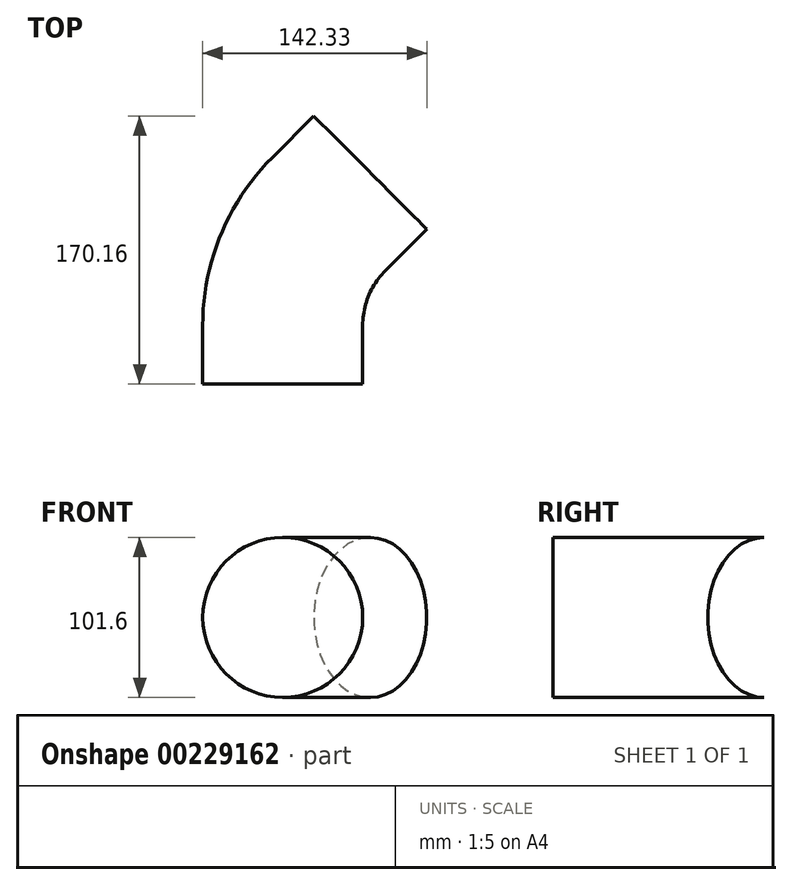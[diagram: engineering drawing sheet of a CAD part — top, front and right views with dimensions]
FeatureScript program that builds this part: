
annotation { "Feature Type Name" : "Feature", "Feature Type Description" : "" }
export const myFeature = defineFeature(function(context is Context, id is Id, definition is map)
    precondition{}
    {
        {
            var Q0;
            Q0=qCreatedBy(makeId("Front.planeOp"),FACE);
            var sketch = newSketch(context, id + "F0", { "sketchPlane" : qUnion([Q0])});
            skCircle(sketch, "E0", {"center": v(1.47, 0) * mm, "radius": 50.8 * mm});
            skSolve(sketch);
        }
        {
            var Q0;
            Q0=qCreatedBy(makeId("Top.planeOp"),FACE);
            var sketch = newSketch(context, id + "F1", { "sketchPlane" : qUnion([Q0])});
            skLineSegment(sketch, "E1", {"start": v(0, 0) * mm, "end": v(0, 37.16) * mm});
            skLineSegment(sketch, "E2", {"start": v(29.76, 109) * mm, "end": v(56.04, 135.28) * mm});
            skPoint(sketch, "E3.visualSharp", {"position": v(0, 79.25) * mm});
            skArc(sketch, "E3.filletArc", {"start": v(29.76, 109) * mm, "mid": v(7.73, 76.04) * mm, "end": v(0, 37.16) * mm});
            skSolve(sketch);
        }
        {
            var Q0;
            Q0=makeQuery(id+"F0.imprint","IMPRINT",FACE,{"disambiguationData":[TD([[makeQuery(id+"F0.imprint","IMPRINT",EDGE,{"derivedFrom":sQuery(id+"F0.wireOp",EDGE,"E0")}),1.0]])]});
            var Q1;
            Q1=sQuery(id+"F1.wireOp",EDGE,"E1");
            var Q2;
            Q2=sQuery(id+"F1.wireOp",EDGE,"E3.filletArc");
            var Q3;
            Q3=sQuery(id+"F1.wireOp",EDGE,"E2");
            sweep(context, id + "F2", {"profiles" : qUnion([Q0]), "path" : qUnion([Q1, Q2, Q3])});
        }
    });
